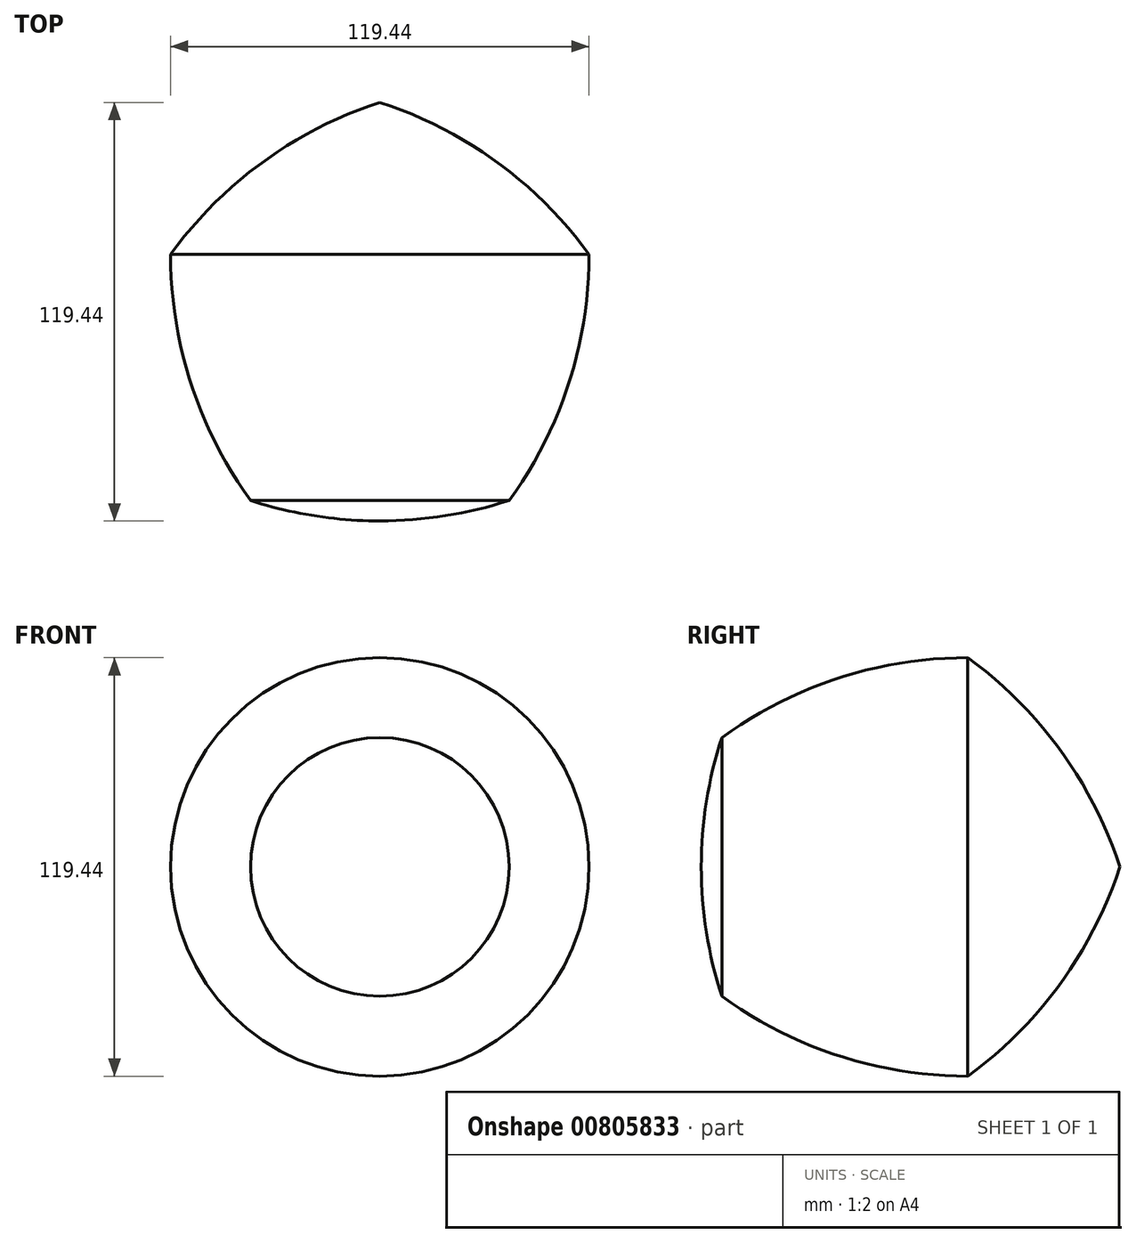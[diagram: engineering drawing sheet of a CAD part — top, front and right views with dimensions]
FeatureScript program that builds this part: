
annotation { "Feature Type Name" : "Feature", "Feature Type Description" : "" }
export const myFeature = defineFeature(function(context is Context, id is Id, definition is map)
    precondition{}
    {
        {
            var Q0;
            Q0=qCreatedBy(makeId("Top.planeOp"),FACE);
            var sketch = newSketch(context, id + "F0", { "sketchPlane" : qUnion([Q0])});
            skCircle(sketch, "E0.cCircle", {"center": v(0, 0) * mm, "radius": 50.8 * mm, "construction": true});
            skLineSegment(sketch, "E0.0", {"start": v(0, 62.8) * mm, "end": v(59.72, 19.4) * mm});
            skLineSegment(sketch, "E0.1", {"start": v(59.72, 19.4) * mm, "end": v(36.9, -50.8) * mm});
            skLineSegment(sketch, "E0.2", {"start": v(36.9, -50.8) * mm, "end": v(-36.9, -50.8) * mm});
            skLineSegment(sketch, "E0.3", {"start": v(-36.9, -50.8) * mm, "end": v(-59.72, 19.4) * mm});
            skLineSegment(sketch, "E0.4", {"start": v(-59.72, 19.4) * mm, "end": v(0, 62.8) * mm});
            skPoint(sketch, "E0.0.midPoint", {"position": v(29.86, 41.1) * mm});
            skCircle(sketch, "E1", {"center": v(-59.72, 19.4) * mm, "radius": 119.44 * mm});
            skCircle(sketch, "E2", {"center": v(-36.9, -50.8) * mm, "radius": 119.44 * mm});
            skCircle(sketch, "E3", {"center": v(36.9, -50.8) * mm, "radius": 119.44 * mm});
            skCircle(sketch, "E4", {"center": v(59.72, 19.4) * mm, "radius": 119.44 * mm});
            skCircle(sketch, "E5", {"center": v(0, 62.8) * mm, "radius": 119.44 * mm});
            skLineSegment(sketch, "E6", {"start": v(0, 101.6) * mm, "end": v(0, -152.4) * mm});
            skPoint(sketch, "E6.endSnap0", {"position": v(0, -50.8) * mm});
            skSolve(sketch);
        }
        {
            var Q0;
            {var subQ0=sQuery(id+"F0.wireOp",EDGE,"E0.4");Q0=makeQuery(id+"F0.imprint","IMPRINT",FACE,{"disambiguationData":[TD([[makeQuery(id+"F0.imprint","IMPRINT",EDGE,{"derivedFrom":subQ0}),1.0]])]});}
            var Q1;
            {var subQ0=sQuery(id+"F0.wireOp",EDGE,"E0.3");Q1=makeQuery(id+"F0.imprint","IMPRINT",FACE,{"disambiguationData":[TD([[makeQuery(id+"F0.imprint","IMPRINT",EDGE,{"derivedFrom":subQ0}),-1.0]])]});}
            var Q2;
            {var subQ0=sQuery(id+"F0.wireOp",EDGE,"E0.3");Q2=makeQuery(id+"F0.imprint","IMPRINT",FACE,{"disambiguationData":[TD([[makeQuery(id+"F0.imprint","IMPRINT",EDGE,{"derivedFrom":subQ0}),1.0]])]});}
            var Q3;
            {var subQ1=sQuery(id+"F0.wireOp",EDGE,"E0.2");var subQ3=sQuery(id+"F0.wireOp",EDGE,"E6");var subQ4=makeQuery(id+"F0.imprint","INTERSECT",VERTEX,{"derivedFrom":[subQ1,subQ3]});Q3=makeQuery(id+"F0.imprint","IMPRINT",FACE,{"disambiguationData":[TD([[makeQuery(id+"F0.imprint","IMPRINT",EDGE,{"disambiguationData":[TD([[subQ4,-1.0]])],"derivedFrom":subQ3}),-1.0]])]});}
            var Q4;
            Q4=sQuery(id+"F0.wireOp",EDGE,"E6");
            revolve(context, id + "F1", {"surfaceOperationType" : NewSurfaceOperationType.NEW, "entities" : qUnion([Q0, Q1, Q2, Q3]), "axis" : qUnion([Q4]), "revolveType" : RevolveType.FULL});
        }
    });
